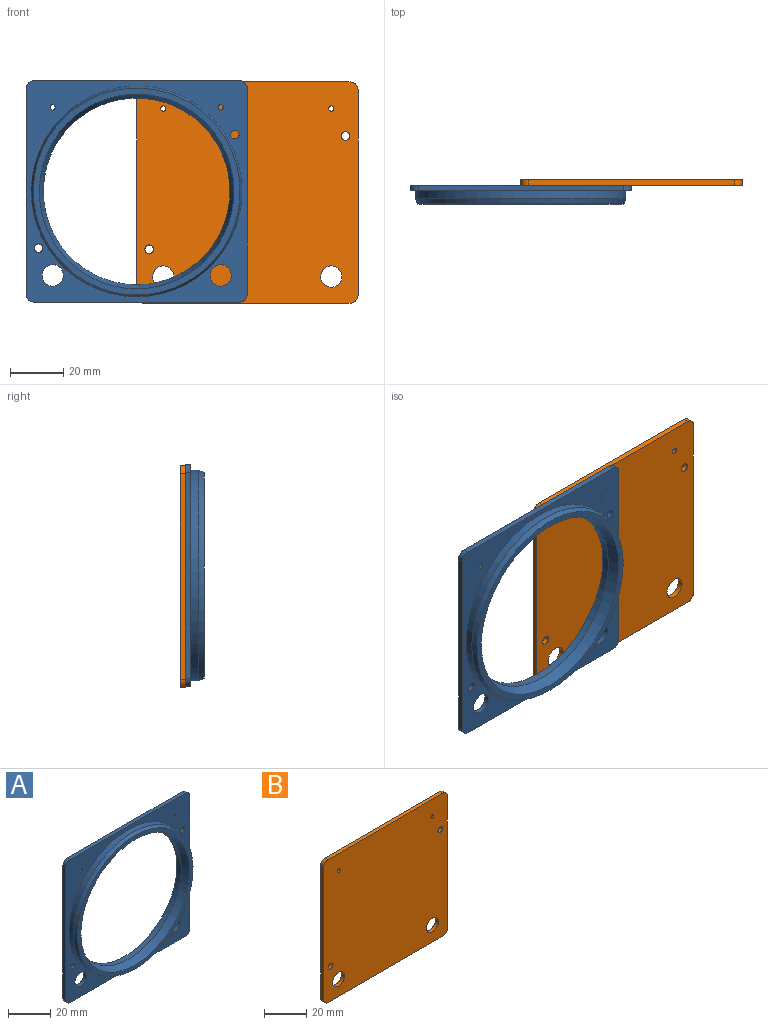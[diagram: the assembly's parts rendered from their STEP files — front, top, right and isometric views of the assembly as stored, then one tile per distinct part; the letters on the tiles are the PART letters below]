
ASSEMBLY  parts=2 mates=1
PART A: 21 faces, bbox 83x7x83 mm
  f0: plane 77x2mm, normal (0,0,1), area 154mm2, adj f1,f12,f13,f14
  f1: cylinder r=3mm len=3mm, axis (0,-1,0), area 9.4mm2, adj f0,f2,f13,f14
  f2: plane 77x2mm, normal (-1,0,0), area 154mm2, adj f1,f3,f13,f14
  f3: cylinder r=3mm len=3mm, axis (0,-1,0), area 9.4mm2, adj f2,f4,f13,f14
  f4: plane 77x2mm, normal (0,0,-1), area 154mm2, adj f3,f5,f13,f14
  f5: cylinder r=3mm len=3mm, axis (0,-1,0), area 9.4mm2, adj f4,f6,f13,f14
  f6: plane 77x2mm, normal (1,0,0), area 154mm2, adj f5,f12,f13,f14
  f7: cylinder r=35mm len=70mm, axis (0,-1,0), area 633.1mm2, adj f13,f20
  f8: cylinder r=1mm len=2mm, axis (0,-1,0), area 12.6mm2, adj f13,f14
  f9: cylinder r=1mm len=2mm, axis (0,-1,0), area 12.6mm2, adj f13,f14
  f10: cylinder r=4mm len=8mm, axis (0,-1,0), area 50.3mm2, adj f13,f14
  f11: cylinder r=4mm len=8mm, axis (0,-1,0), area 50.3mm2, adj f13,f14
  f12: cylinder r=3mm len=3mm, axis (0,-1,0), area 9.4mm2, adj f0,f6,f13,f14
  f13: plane 83x83mm, normal (0,1,0), area 2909.9mm2, adj f0,f1,f2,f3,f4,f5,f6,f7
  f14: plane 83x83mm, normal (0,-1,0), area 1856.7mm2, adj f0,f1,f2,f3,f4,f5,f6,f8
  f15: cylinder r=1.6mm len=3.2mm, axis (0,-1,0), area 20.1mm2, adj f13,f14
  f16: cylinder r=1.6mm len=3.2mm, axis (0,-1,0), area 20.1mm2, adj f13,f14
  f17: cylinder r=39.5mm len=79mm, axis (0,1,0), area 744.6mm2, adj f14,f19
  f18: plane 77.54x77.54mm, normal (0,-1,0), area 537.3mm2, adj f19,f20
  f19: cone r=38.77mm half-angle=20deg, axis (0,1,0), area 523.4mm2, adj f17,f18
  f20: cone r=35mm half-angle=20deg, axis (0,-1,0), area 985.1mm2, adj f7,f18
PART B: 16 faces, bbox 83x2x83 mm
  f0: plane 77x2mm, normal (0,0,1), area 154mm2, adj f1,f11,f12,f13
  f1: cylinder r=3mm len=3mm, axis (0,-1,0), area 9.4mm2, adj f0,f2,f12,f13
  f2: plane 77x2mm, normal (-1,0,0), area 154mm2, adj f1,f3,f12,f13
  f3: cylinder r=3mm len=3mm, axis (0,-1,0), area 9.4mm2, adj f2,f4,f12,f13
  f4: plane 77x2mm, normal (0,0,-1), area 154mm2, adj f3,f5,f12,f13
  f5: cylinder r=3mm len=3mm, axis (0,-1,0), area 9.4mm2, adj f4,f6,f12,f13
  f6: plane 77x2mm, normal (1,0,0), area 154mm2, adj f5,f11,f12,f13
  f7: cylinder r=1mm len=2mm, axis (0,-1,0), area 12.6mm2, adj f12,f13
  f8: cylinder r=1mm len=2mm, axis (0,-1,0), area 12.6mm2, adj f12,f13
  f9: cylinder r=4mm len=8mm, axis (0,-1,0), area 50.3mm2, adj f12,f13
  f10: cylinder r=4mm len=8mm, axis (0,-1,0), area 50.3mm2, adj f12,f13
  f11: cylinder r=3mm len=3mm, axis (0,-1,0), area 9.4mm2, adj f0,f6,f12,f13
  f12: plane 83x83mm, normal (0,1,0), area 6758.4mm2, adj f0,f1,f2,f3,f4,f5,f6,f7
  f13: plane 83x83mm, normal (0,-1,0), area 6758.4mm2, adj f0,f1,f2,f3,f4,f5,f6,f7
  f14: cylinder r=1.6mm len=3.2mm, axis (0,-1,0), area 20.1mm2, adj f12,f13
  f15: cylinder r=1.6mm len=3.2mm, axis (0,-1,0), area 20.1mm2, adj f12,f13
PLACE A t=(-35.9,39.29,-37)mm
PLACE B t=(5.6,41.29,-37.44)mm
MATE fastened A.f13 <-> B.f13  axis (0,1,0) through (5.6,41.29,-37)mm
